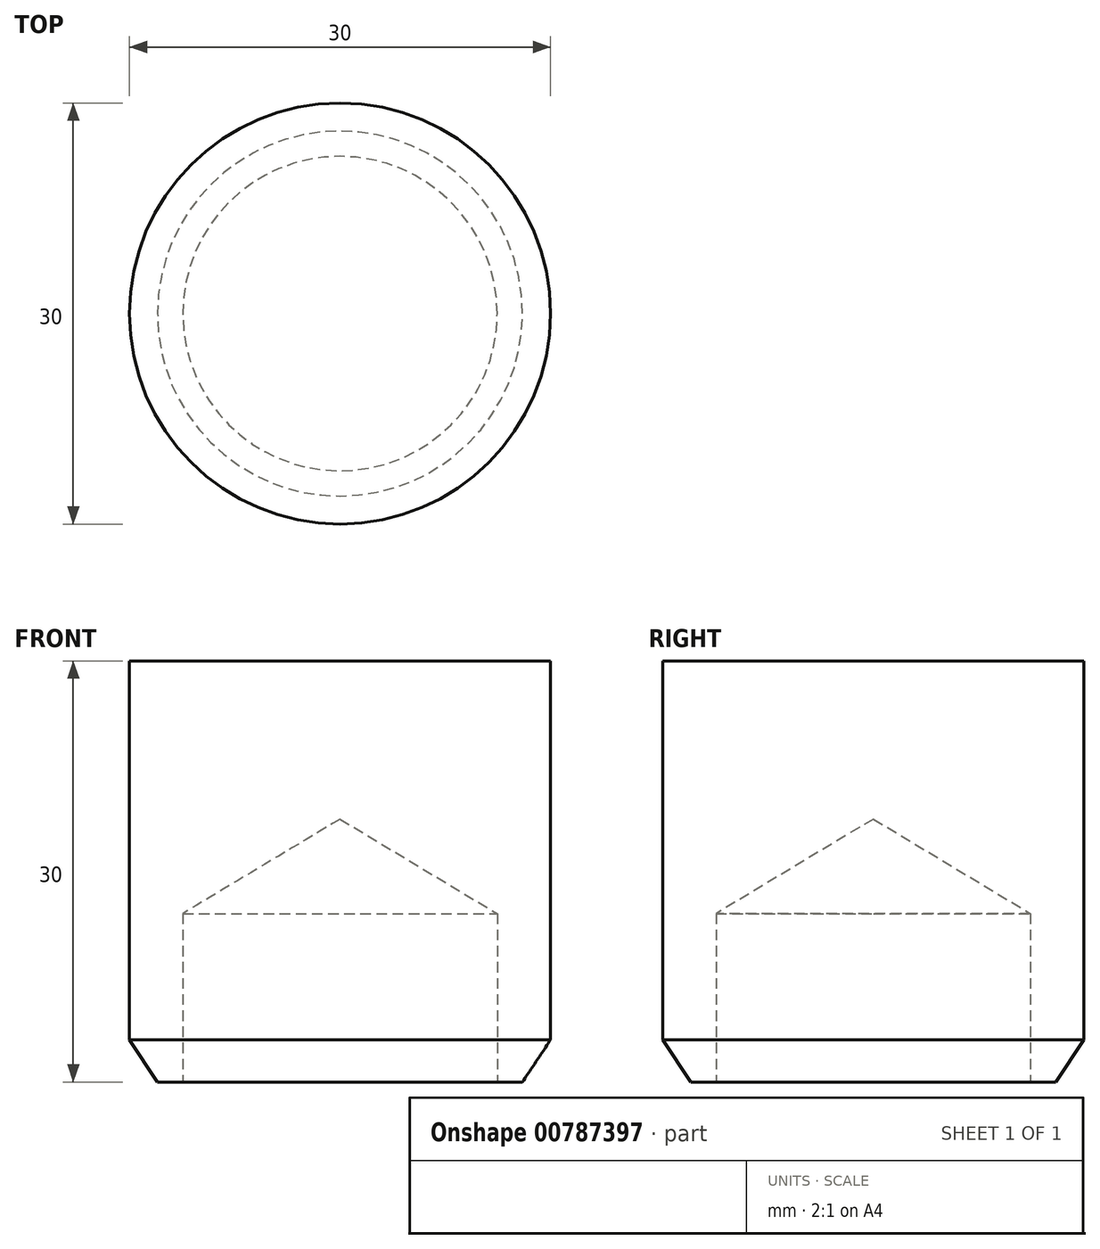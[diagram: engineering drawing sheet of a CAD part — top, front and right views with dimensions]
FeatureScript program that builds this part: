
annotation { "Feature Type Name" : "Feature", "Feature Type Description" : "" }
export const myFeature = defineFeature(function(context is Context, id is Id, definition is map)
    precondition{}
    {
        {
            var Q0;
            Q0=qCreatedBy(makeId("Top.planeOp"),FACE);
            var sketch = newSketch(context, id + "F0", { "sketchPlane" : qUnion([Q0])});
            skCircle(sketch, "E0", {"center": v(0, 0) * mm, "radius": 15 * mm});
            skSolve(sketch);
        }
        {
            var Q0;
            Q0 = qSketchRegion(id + "F0", true);
            extrude(context, id + "F1", {"entities" : qUnion([Q0]), "depth" : 30 * mm, "offsetDistance" : 25 * mm});
        }
        {
            var Q0;
            Q0=makeQuery(id+"F1.opExtrude","CAP_FACE",FACE,{"disambiguationData":[OSD([sQuery(id+"F0.wireOp",EDGE,"E0")])],"isStart":true});
            var sketch = newSketch(context, id + "F2", { "sketchPlane" : qUnion([Q0])});
            skCircle(sketch, "E1", {"center": v(0, 0) * mm, "radius": 12.8 * mm});
            skSolve(sketch);
        }
        {
            var Q0;
            Q0=sQuery(id+"F2.wireOp",VERTEX,"E1.center");
            var Q1;
            Q1=makeQuery(id+"F1.opExtrude","SWEPT_BODY",BODY,{"disambiguationData":[OSD([sQuery(id+"F0.wireOp",EDGE,"E0")])]});
            hole(context, id + "F3", {"style" : HoleStyle.SIMPLE, "endStyle" : HoleEndStyle.BLIND, "holeDiameter" : 22.4 * mm, "majorDiameter" : 5 * mm, "holeDepth" : 12 * mm, "isTappedThrough" : true, "tappedDepth" : 12 * mm, "tapClearance" : 3, "locations" : qUnion([Q0]), "scope" : qUnion([Q1])});
        }
        {
            var Q0;
            Q0=makeQuery(id+"F1.opExtrude","CAP_EDGE",EDGE,{"disambiguationData":[OSD([sQuery(id+"F0.wireOp",EDGE,"E0")])],"isStart":true});
            chamfer(context, id + "F4", {"entities" : qUnion([Q0]), "chamferType" : ChamferType.TWO_OFFSETS, "width1" : 3 * mm, "oppositeDirection" : false, "width2" : 2 * mm, "tangentPropagation" : true});
        }
    });
